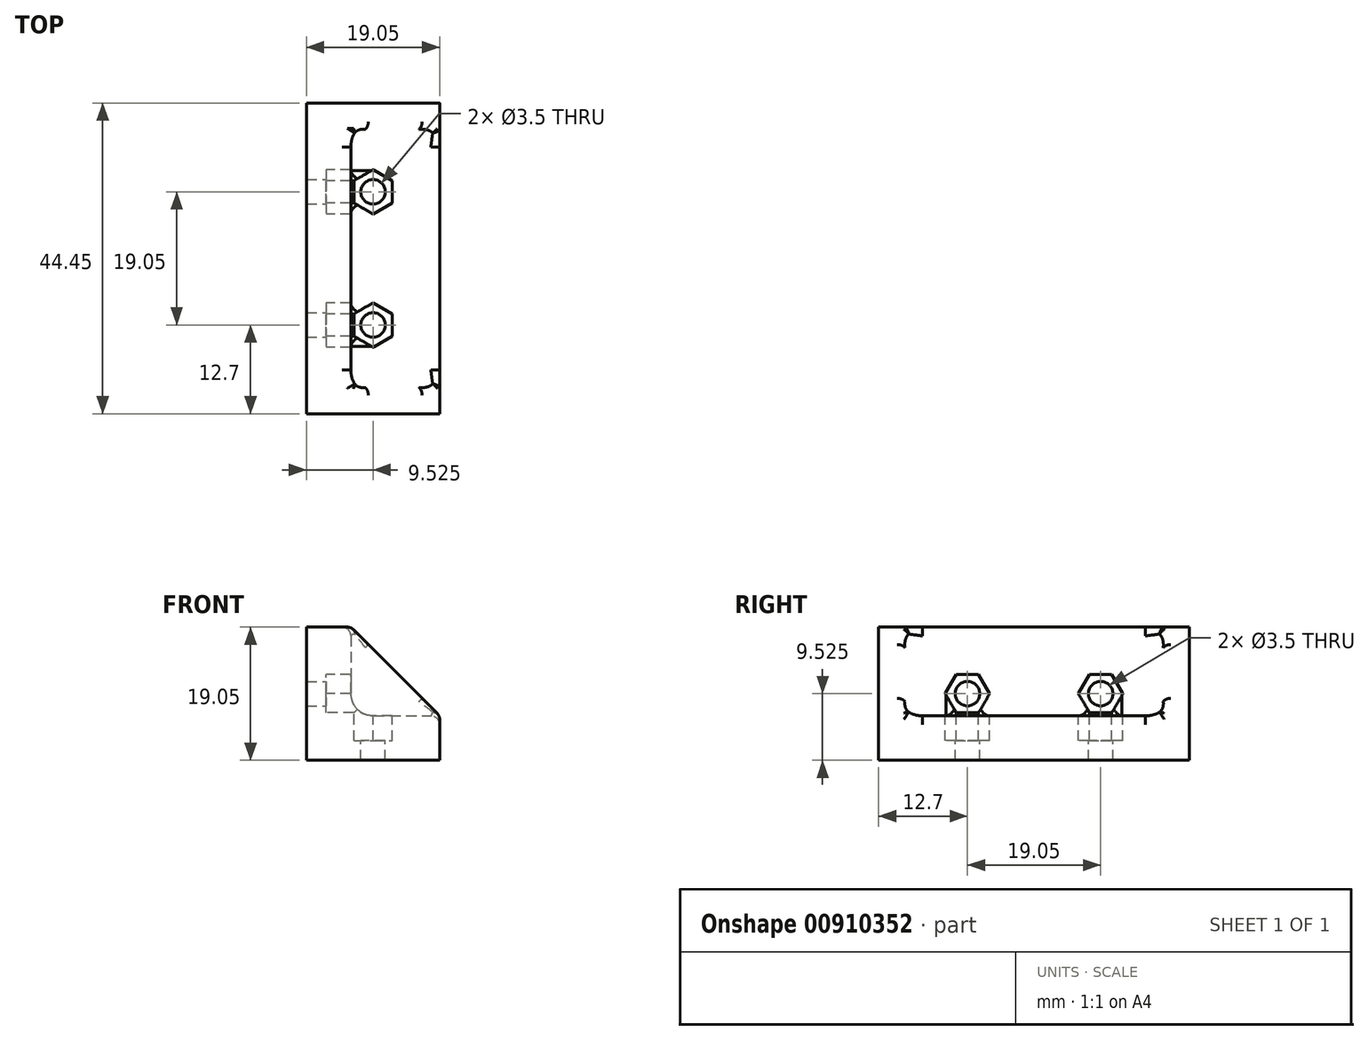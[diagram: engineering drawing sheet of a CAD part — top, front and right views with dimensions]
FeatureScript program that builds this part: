
annotation { "Feature Type Name" : "Feature", "Feature Type Description" : "" }
export const myFeature = defineFeature(function(context is Context, id is Id, definition is map)
    precondition{}
    {
        {
            var Q0;
            Q0=qCreatedBy(makeId("Front.planeOp"),FACE);
            var sketch = newSketch(context, id + "F0", { "sketchPlane" : qUnion([Q0])});
            skLineSegment(sketch, "E0", {"start": v(0, 19.05) * mm, "end": v(0, 0) * mm});
            skLineSegment(sketch, "E1", {"start": v(0, 0) * mm, "end": v(19.05, 0) * mm});
            skLineSegment(sketch, "E2", {"start": v(19.05, 0) * mm, "end": v(19.05, 6.35) * mm});
            skLineSegment(sketch, "E3", {"start": v(19.05, 6.35) * mm, "end": v(6.35, 6.35) * mm});
            skLineSegment(sketch, "E4", {"start": v(6.35, 6.35) * mm, "end": v(6.35, 19.05) * mm});
            skLineSegment(sketch, "E5", {"start": v(6.35, 19.05) * mm, "end": v(0, 19.05) * mm});
            skSolve(sketch);
        }
        {
            var Q0;
            Q0 = qSketchRegion(id + "F0", true);
            extrude(context, id + "F1", {"entities" : qUnion([Q0]), "depth" : 44.45 * mm, "offsetDistance" : 25.4 * mm});
        }
        {
            var Q0;
            Q0=makeQuery(id+"F1.opExtrude","CAP_FACE",FACE,{"disambiguationData":[OSD([sQuery(id+"F0.wireOp",EDGE,"E0"),sQuery(id+"F0.wireOp",EDGE,"E1"),sQuery(id+"F0.wireOp",EDGE,"E2"),sQuery(id+"F0.wireOp",EDGE,"E3"),sQuery(id+"F0.wireOp",EDGE,"E4"),sQuery(id+"F0.wireOp",EDGE,"E5")])],"isStart":false});
            var sketch = newSketch(context, id + "F2", { "sketchPlane" : qUnion([Q0])});
            skLineSegment(sketch, "E6.0", {"start": v(19.05, 6.35) * mm, "end": v(6.35, 6.35) * mm});
            skLineSegment(sketch, "E6.1", {"start": v(6.35, 6.35) * mm, "end": v(6.35, 19.05) * mm});
            skLineSegment(sketch, "E7", {"start": v(19.05, 6.35) * mm, "end": v(6.35, 19.05) * mm});
            skSolve(sketch);
        }
        {
            var Q0;
            Q0 = qSketchRegion(id + "F2", true);
            extrude(context, id + "F3", {"entities" : qUnion([Q0]), "operationType" : NewBodyOperationType.ADD, "oppositeDirection" : true, "depth" : 8.9 * mm, "offsetDistance" : 25.4 * mm});
        }
        {
            var Q0;
            Q0=makeQuery(id+"F1.opExtrude","CAP_FACE",FACE,{"disambiguationData":[OSD([sQuery(id+"F0.wireOp",EDGE,"E0"),sQuery(id+"F0.wireOp",EDGE,"E1"),sQuery(id+"F0.wireOp",EDGE,"E2"),sQuery(id+"F0.wireOp",EDGE,"E3"),sQuery(id+"F0.wireOp",EDGE,"E4"),sQuery(id+"F0.wireOp",EDGE,"E5")])],"isStart":true});
            var sketch = newSketch(context, id + "F4", { "sketchPlane" : qUnion([Q0])});
            skLineSegment(sketch, "E8.0", {"start": v(-19.05, 6.35) * mm, "end": v(-6.35, 6.35) * mm});
            skLineSegment(sketch, "E8.1", {"start": v(-6.35, 6.35) * mm, "end": v(-6.35, 19.05) * mm});
            skLineSegment(sketch, "E9", {"start": v(-19.05, 6.35) * mm, "end": v(-6.35, 19.05) * mm});
            skSolve(sketch);
        }
        {
            var Q0;
            Q0 = qSketchRegion(id + "F4", true);
            extrude(context, id + "F5", {"entities" : qUnion([Q0]), "operationType" : NewBodyOperationType.ADD, "oppositeDirection" : true, "depth" : 8.9 * mm, "offsetDistance" : 25.4 * mm});
        }
        {
            var Q0;
            Q0=makeQuery(id+"F5.opExtrude","CAP_EDGE",EDGE,{"disambiguationData":[OSD([sQuery(id+"F4.wireOp",EDGE,"E9")])],"isStart":false});
            chamfer(context, id + "F6", {"entities" : qUnion([Q0]), "chamferType" : ChamferType.OFFSET_ANGLE, "width" : 9.52 * mm, "oppositeDirection" : false, "angle" : 30 * degree, "tangentPropagation" : true});
        }
        {
            var Q0;
            Q0=makeQuery(id+"F3.opExtrude","CAP_EDGE",EDGE,{"disambiguationData":[OSD([sQuery(id+"F2.wireOp",EDGE,"E7")])],"isStart":false});
            chamfer(context, id + "F7", {"entities" : qUnion([Q0]), "chamferType" : ChamferType.OFFSET_ANGLE, "width" : 9.52 * mm, "oppositeDirection" : true, "angle" : 30 * degree, "tangentPropagation" : true});
        }
        {
            var Q0;
            Q0=makeQuery(id+"F1.opExtrude","SWEPT_FACE",FACE,{"disambiguationData":[OSD([sQuery(id+"F0.wireOp",EDGE,"E1")])]});
            var sketch = newSketch(context, id + "F8", { "sketchPlane" : qUnion([Q0])});
            skPoint(sketch, "E10", {"position": v(9.53, 31.75) * mm});
            skPoint(sketch, "E11", {"position": v(9.53, 12.7) * mm});
            skLineSegment(sketch, "E12", {"start": v(9.53, 0) * mm, "end": v(9.53, 12.7) * mm, "construction": true});
            skLineSegment(sketch, "E13", {"start": v(9.52, 31.75) * mm, "end": v(9.53, 12.7) * mm, "construction": true});
            skLineSegment(sketch, "E14", {"start": v(9.52, 31.75) * mm, "end": v(9.52, 44.45) * mm, "construction": true});
            skSolve(sketch);
        }
        {
            var Q0;
            Q0=makeQuery(id+"F1.opExtrude","SWEPT_FACE",FACE,{"disambiguationData":[OSD([sQuery(id+"F0.wireOp",EDGE,"E0")])]});
            var sketch = newSketch(context, id + "F9", { "sketchPlane" : qUnion([Q0])});
            skLineSegment(sketch, "E15", {"start": v(44.45, 9.53) * mm, "end": v(31.75, 9.53) * mm, "construction": true});
            skLineSegment(sketch, "E16", {"start": v(31.75, 9.53) * mm, "end": v(12.7, 9.53) * mm, "construction": true});
            skLineSegment(sketch, "E17", {"start": v(12.7, 9.53) * mm, "end": v(0, 9.53) * mm, "construction": true});
            skSolve(sketch);
        }
        {
            var Q0;
            Q0=makeQuery(id+"F1.opExtrude","SWEPT_EDGE",EDGE,{"disambiguationData":[OSD([sQuery(id+"F0.wireOp",EDGE,"E3"),sQuery(id+"F0.wireOp",EDGE,"E4")])]});
            var Q1;
            Q1=makeQuery(id+"F6.opChamfer","BLEND_EDGE",EDGE,{"blendedFrom":[makeQuery(id+"F5.opExtrude","CAP_EDGE",EDGE,{"disambiguationData":[OSD([sQuery(id+"F4.wireOp",EDGE,"E9")])],"isStart":false}),makeQuery(id+"F1.opExtrude","SWEPT_FACE",FACE,{"disambiguationData":[OSD([sQuery(id+"F0.wireOp",EDGE,"E4")])]})],"blendedInto":[makeQuery(id+"F1.opExtrude","SWEPT_FACE",FACE,{"disambiguationData":[OSD([sQuery(id+"F0.wireOp",EDGE,"E4")])]})]});
            var Q2;
            Q2=makeQuery(id+"F6.opChamfer","BLEND_EDGE",EDGE,{"blendedFrom":[makeQuery(id+"F5.opExtrude","CAP_EDGE",EDGE,{"disambiguationData":[OSD([sQuery(id+"F4.wireOp",EDGE,"E9")])],"isStart":false}),makeQuery(id+"F1.opExtrude","SWEPT_FACE",FACE,{"disambiguationData":[OSD([sQuery(id+"F0.wireOp",EDGE,"E3")])]})],"blendedInto":[makeQuery(id+"F1.opExtrude","SWEPT_FACE",FACE,{"disambiguationData":[OSD([sQuery(id+"F0.wireOp",EDGE,"E3")])]})]});
            var Q3;
            Q3=makeQuery(id+"F7.opChamfer","BLEND_EDGE",EDGE,{"blendedFrom":[makeQuery(id+"F3.opExtrude","CAP_EDGE",EDGE,{"disambiguationData":[OSD([sQuery(id+"F2.wireOp",EDGE,"E7")])],"isStart":false}),makeQuery(id+"F1.opExtrude","SWEPT_FACE",FACE,{"disambiguationData":[OSD([sQuery(id+"F0.wireOp",EDGE,"E3")])]})],"blendedInto":[makeQuery(id+"F1.opExtrude","SWEPT_FACE",FACE,{"disambiguationData":[OSD([sQuery(id+"F0.wireOp",EDGE,"E3")])]})]});
            var Q4;
            Q4=makeQuery(id+"F7.opChamfer","BLEND_EDGE",EDGE,{"blendedFrom":[makeQuery(id+"F3.opExtrude","CAP_EDGE",EDGE,{"disambiguationData":[OSD([sQuery(id+"F2.wireOp",EDGE,"E7")])],"isStart":false}),makeQuery(id+"F1.opExtrude","SWEPT_FACE",FACE,{"disambiguationData":[OSD([sQuery(id+"F0.wireOp",EDGE,"E4")])]})],"blendedInto":[makeQuery(id+"F1.opExtrude","SWEPT_FACE",FACE,{"disambiguationData":[OSD([sQuery(id+"F0.wireOp",EDGE,"E4")])]})]});
            fillet(context, id + "F10", {"entities" : qUnion([Q0, Q1, Q2, Q3, Q4]), "radius" : 3.17 * mm, "tangentPropagation" : true, "allowEdgeOverflow" : false});
        }
        {
            var Q0;
            {var subQ0=sQuery(id+"F0.wireOp",EDGE,"E5");var subQ1=makeQuery(id+"F1.opExtrude","SWEPT_EDGE",EDGE,{"disambiguationData":[OSD([sQuery(id+"F0.wireOp",EDGE,"E4"),subQ0])]});var subQ2=makeQuery(id+"F3.boolean.opBoolean","SPLIT",EDGE,{"derivedFrom":subQ1});Q0=makeQuery(id+"F7.opChamfer","MERGE",EDGE,{"derivedFrom":[makeQuery(id+"F3.boolean.opBoolean","MERGE",EDGE,{"derivedFrom":[subQ1,makeQuery(id+"F3.opExtrude","SWEPT_EDGE",EDGE,{"disambiguationData":[OSD([subQ0,sQuery(id+"F2.wireOp",EDGE,"E6.1"),sQuery(id+"F2.wireOp",EDGE,"E7")])]})]}),makeQuery(id+"F6.opChamfer","MERGE",EDGE,{"derivedFrom":[makeQuery(id+"F5.boolean.opBoolean","MERGE",EDGE,{"derivedFrom":[subQ2,makeQuery(id+"F5.opExtrude","SWEPT_EDGE",EDGE,{"disambiguationData":[OSD([subQ0,sQuery(id+"F4.wireOp",EDGE,"E8.1"),sQuery(id+"F4.wireOp",EDGE,"E9")])]})]}),makeQuery(id+"F5.boolean.opBoolean","SPLIT",EDGE,{"derivedFrom":subQ2})]})]});}
            var Q1;
            {var subQ0=sQuery(id+"F0.wireOp",EDGE,"E2");var subQ1=makeQuery(id+"F1.opExtrude","SWEPT_EDGE",EDGE,{"disambiguationData":[OSD([subQ0,sQuery(id+"F0.wireOp",EDGE,"E3")])]});var subQ2=makeQuery(id+"F3.boolean.opBoolean","SPLIT",EDGE,{"derivedFrom":subQ1});Q1=makeQuery(id+"F7.opChamfer","MERGE",EDGE,{"derivedFrom":[makeQuery(id+"F3.boolean.opBoolean","MERGE",EDGE,{"derivedFrom":[subQ1,makeQuery(id+"F3.opExtrude","SWEPT_EDGE",EDGE,{"disambiguationData":[OSD([subQ0,sQuery(id+"F2.wireOp",EDGE,"E6.0"),sQuery(id+"F2.wireOp",EDGE,"E7")])]})]}),makeQuery(id+"F6.opChamfer","MERGE",EDGE,{"derivedFrom":[makeQuery(id+"F5.boolean.opBoolean","MERGE",EDGE,{"derivedFrom":[subQ2,makeQuery(id+"F5.opExtrude","SWEPT_EDGE",EDGE,{"disambiguationData":[OSD([subQ0,sQuery(id+"F4.wireOp",EDGE,"E8.0"),sQuery(id+"F4.wireOp",EDGE,"E9")])]})]}),makeQuery(id+"F5.boolean.opBoolean","SPLIT",EDGE,{"derivedFrom":subQ2})]})]});}
            var Q2;
            {var subQ0=sQuery(id+"F4.wireOp",EDGE,"E9");Q2=makeQuery(id+"F6.opChamfer","BLEND_EDGE",EDGE,{"blendedFrom":[makeQuery(id+"F5.opExtrude","CAP_EDGE",EDGE,{"disambiguationData":[OSD([subQ0])],"isStart":false}),makeQuery(id+"F5.opExtrude","SWEPT_FACE",FACE,{"disambiguationData":[OSD([subQ0])]})],"blendedInto":[makeQuery(id+"F5.opExtrude","SWEPT_FACE",FACE,{"disambiguationData":[OSD([subQ0])]})]});}
            var Q3;
            {var subQ0=sQuery(id+"F2.wireOp",EDGE,"E7");Q3=makeQuery(id+"F7.opChamfer","BLEND_EDGE",EDGE,{"blendedFrom":[makeQuery(id+"F3.opExtrude","CAP_EDGE",EDGE,{"disambiguationData":[OSD([subQ0])],"isStart":false}),makeQuery(id+"F3.opExtrude","SWEPT_FACE",FACE,{"disambiguationData":[OSD([subQ0])]})],"blendedInto":[makeQuery(id+"F3.opExtrude","SWEPT_FACE",FACE,{"disambiguationData":[OSD([subQ0])]})]});}
            fillet(context, id + "F11", {"entities" : qUnion([Q0, Q1, Q2, Q3]), "radius" : 1.27 * mm, "tangentPropagation" : true, "allowEdgeOverflow" : false});
        }
        {
            var Q0;
            {var subQ0=sQuery(id+"F0.wireOp",EDGE,"E2");Q0=makeQuery(id+"F5.boolean.opBoolean","MERGE",EDGE,{"derivedFrom":[makeQuery(id+"F3.boolean.opBoolean","SPLIT",EDGE,{"derivedFrom":makeQuery(id+"F1.opExtrude","SWEPT_EDGE",EDGE,{"disambiguationData":[OSD([subQ0,sQuery(id+"F0.wireOp",EDGE,"E3")])]})}),makeQuery(id+"F5.opExtrude","SWEPT_EDGE",EDGE,{"disambiguationData":[OSD([subQ0,sQuery(id+"F4.wireOp",EDGE,"E8.0"),sQuery(id+"F4.wireOp",EDGE,"E9")])]})]});}
            var Q1;
            {var subQ0=sQuery(id+"F0.wireOp",EDGE,"E5");Q1=makeQuery(id+"F5.boolean.opBoolean","MERGE",EDGE,{"derivedFrom":[makeQuery(id+"F3.boolean.opBoolean","SPLIT",EDGE,{"derivedFrom":makeQuery(id+"F1.opExtrude","SWEPT_EDGE",EDGE,{"disambiguationData":[OSD([sQuery(id+"F0.wireOp",EDGE,"E4"),subQ0])]})}),makeQuery(id+"F5.opExtrude","SWEPT_EDGE",EDGE,{"disambiguationData":[OSD([subQ0,sQuery(id+"F4.wireOp",EDGE,"E8.1"),sQuery(id+"F4.wireOp",EDGE,"E9")])]})]});}
            var Q2;
            {var subQ0=sQuery(id+"F0.wireOp",EDGE,"E5");Q2=makeQuery(id+"F7.opChamfer","SPLIT",EDGE,{"derivedFrom":makeQuery(id+"F3.boolean.opBoolean","MERGE",EDGE,{"derivedFrom":[makeQuery(id+"F1.opExtrude","SWEPT_EDGE",EDGE,{"disambiguationData":[OSD([sQuery(id+"F0.wireOp",EDGE,"E4"),subQ0])]}),makeQuery(id+"F3.opExtrude","SWEPT_EDGE",EDGE,{"disambiguationData":[OSD([subQ0,sQuery(id+"F2.wireOp",EDGE,"E6.1"),sQuery(id+"F2.wireOp",EDGE,"E7")])]})]})});}
            var Q3;
            {var subQ0=sQuery(id+"F0.wireOp",EDGE,"E2");Q3=makeQuery(id+"F7.opChamfer","SPLIT",EDGE,{"derivedFrom":makeQuery(id+"F3.boolean.opBoolean","MERGE",EDGE,{"derivedFrom":[makeQuery(id+"F1.opExtrude","SWEPT_EDGE",EDGE,{"disambiguationData":[OSD([subQ0,sQuery(id+"F0.wireOp",EDGE,"E3")])]}),makeQuery(id+"F3.opExtrude","SWEPT_EDGE",EDGE,{"disambiguationData":[OSD([subQ0,sQuery(id+"F2.wireOp",EDGE,"E6.0"),sQuery(id+"F2.wireOp",EDGE,"E7")])]})]})});}
            fillet(context, id + "F12", {"entities" : qUnion([Q0, Q1, Q2, Q3]), "radius" : 1.27 * mm, "tangentPropagation" : true, "allowEdgeOverflow" : false});
        }
        {
            var Q0;
            Q0=sQuery(id+"F8.wireOp",VERTEX,"E13.start");
            var Q1;
            Q1=sQuery(id+"F9.wireOp",VERTEX,"E15.end");
            var Q2;
            Q2=sQuery(id+"F9.wireOp",VERTEX,"E16.end");
            var Q3;
            Q3=sQuery(id+"F8.wireOp",VERTEX,"E11");
            var Q4;
            Q4=makeQuery(id+"F1.opExtrude","SWEPT_BODY",BODY,{"disambiguationData":[OSD([sQuery(id+"F0.wireOp",EDGE,"E0"),sQuery(id+"F0.wireOp",EDGE,"E1"),sQuery(id+"F0.wireOp",EDGE,"E2"),sQuery(id+"F0.wireOp",EDGE,"E3"),sQuery(id+"F0.wireOp",EDGE,"E4"),sQuery(id+"F0.wireOp",EDGE,"E5")])]});
            hole(context, id + "F13", {"style" : HoleStyle.SIMPLE, "endStyle" : HoleEndStyle.THROUGH, "holeDiameter" : 3.5 * mm, "majorDiameter" : 6.35 * mm, "isTappedThrough" : true, "tappedDepth" : 12.7 * mm, "tapClearance" : 3, "locations" : qUnion([Q0, Q1, Q2, Q3]), "scope" : qUnion([Q4])});
        }
        {
            var Q0;
            Q0=makeQuery(id+"F1.opExtrude","SWEPT_FACE",FACE,{"disambiguationData":[OSD([sQuery(id+"F0.wireOp",EDGE,"E4")])]});
            var sketch = newSketch(context, id + "F14", { "sketchPlane" : qUnion([Q0])});
            skCircle(sketch, "E18.cCircle", {"center": v(-31.75, 9.53) * mm, "radius": 2.75 * mm, "construction": true});
            skLineSegment(sketch, "E18.0", {"start": v(-30.16, 6.77) * mm, "end": v(-33.34, 6.77) * mm});
            skLineSegment(sketch, "E18.1", {"start": v(-33.34, 6.77) * mm, "end": v(-34.93, 9.52) * mm});
            skLineSegment(sketch, "E18.2", {"start": v(-34.93, 9.52) * mm, "end": v(-33.34, 12.27) * mm});
            skLineSegment(sketch, "E18.3", {"start": v(-33.34, 12.27) * mm, "end": v(-30.16, 12.27) * mm});
            skLineSegment(sketch, "E18.4", {"start": v(-30.16, 12.28) * mm, "end": v(-28.57, 9.53) * mm});
            skLineSegment(sketch, "E18.5", {"start": v(-28.57, 9.53) * mm, "end": v(-30.16, 6.78) * mm});
            skPoint(sketch, "E18.0.midPoint", {"position": v(-31.75, 6.78) * mm});
            skCircle(sketch, "E19.cCircle", {"center": v(-12.7, 9.53) * mm, "radius": 2.75 * mm, "construction": true});
            skLineSegment(sketch, "E19.0", {"start": v(-11.11, 6.77) * mm, "end": v(-14.29, 6.77) * mm});
            skLineSegment(sketch, "E19.1", {"start": v(-14.29, 6.78) * mm, "end": v(-15.88, 9.52) * mm});
            skLineSegment(sketch, "E19.2", {"start": v(-15.88, 9.52) * mm, "end": v(-14.29, 12.27) * mm});
            skLineSegment(sketch, "E19.3", {"start": v(-14.29, 12.27) * mm, "end": v(-11.11, 12.27) * mm});
            skLineSegment(sketch, "E19.4", {"start": v(-11.11, 12.28) * mm, "end": v(-9.52, 9.53) * mm});
            skLineSegment(sketch, "E19.5", {"start": v(-9.52, 9.53) * mm, "end": v(-11.11, 6.77) * mm});
            skPoint(sketch, "E19.0.midPoint", {"position": v(-12.7, 6.77) * mm});
            skSolve(sketch);
        }
        {
            var Q0;
            Q0 = qSketchRegion(id + "F14", true);
            extrude(context, id + "F15", {"entities" : qUnion([Q0]), "operationType" : NewBodyOperationType.REMOVE, "depth" : 25.4 * mm, "offsetDistance" : 25.4 * mm, "hasSecondDirection" : true, "secondDirectionOppositeDirection" : true, "secondDirectionDepth" : 3.56 * mm});
        }
        {
            var Q0;
            Q0=makeQuery(id+"F1.opExtrude","SWEPT_FACE",FACE,{"disambiguationData":[OSD([sQuery(id+"F0.wireOp",EDGE,"E3")])]});
            var sketch = newSketch(context, id + "F16", { "sketchPlane" : qUnion([Q0])});
            skCircle(sketch, "E20.cCircle", {"center": v(9.53, -31.75) * mm, "radius": 2.75 * mm, "construction": true});
            skLineSegment(sketch, "E20.0", {"start": v(12.27, -30.16) * mm, "end": v(12.27, -33.34) * mm});
            skLineSegment(sketch, "E20.1", {"start": v(12.27, -33.34) * mm, "end": v(9.53, -34.93) * mm});
            skLineSegment(sketch, "E20.2", {"start": v(9.52, -34.93) * mm, "end": v(6.78, -33.34) * mm});
            skLineSegment(sketch, "E20.3", {"start": v(6.78, -33.34) * mm, "end": v(6.78, -30.16) * mm});
            skLineSegment(sketch, "E20.4", {"start": v(6.78, -30.16) * mm, "end": v(9.53, -28.57) * mm});
            skLineSegment(sketch, "E20.5", {"start": v(9.53, -28.57) * mm, "end": v(12.27, -30.16) * mm});
            skPoint(sketch, "E20.0.midPoint", {"position": v(12.27, -31.75) * mm});
            skCircle(sketch, "E21.cCircle", {"center": v(9.53, -12.7) * mm, "radius": 2.75 * mm, "construction": true});
            skLineSegment(sketch, "E21.0", {"start": v(12.27, -11.11) * mm, "end": v(12.27, -14.29) * mm});
            skLineSegment(sketch, "E21.1", {"start": v(12.27, -14.29) * mm, "end": v(9.53, -15.88) * mm});
            skLineSegment(sketch, "E21.2", {"start": v(9.53, -15.88) * mm, "end": v(6.78, -14.29) * mm});
            skLineSegment(sketch, "E21.3", {"start": v(6.78, -14.29) * mm, "end": v(6.78, -11.11) * mm});
            skLineSegment(sketch, "E21.4", {"start": v(6.78, -11.11) * mm, "end": v(9.53, -9.52) * mm});
            skLineSegment(sketch, "E21.5", {"start": v(9.53, -9.52) * mm, "end": v(12.27, -11.11) * mm});
            skPoint(sketch, "E21.0.midPoint", {"position": v(12.27, -12.7) * mm});
            skSolve(sketch);
        }
        {
            var Q0;
            Q0 = qSketchRegion(id + "F16", true);
            extrude(context, id + "F17", {"entities" : qUnion([Q0]), "operationType" : NewBodyOperationType.REMOVE, "oppositeDirection" : true, "depth" : 3.56 * mm, "offsetDistance" : 25.4 * mm, "hasSecondDirection" : true, "secondDirectionBound" : BoundingType.THROUGH_ALL, "secondDirectionOppositeDirection" : false, "secondDirectionDepth" : 25.4 * mm});
        }
    });
